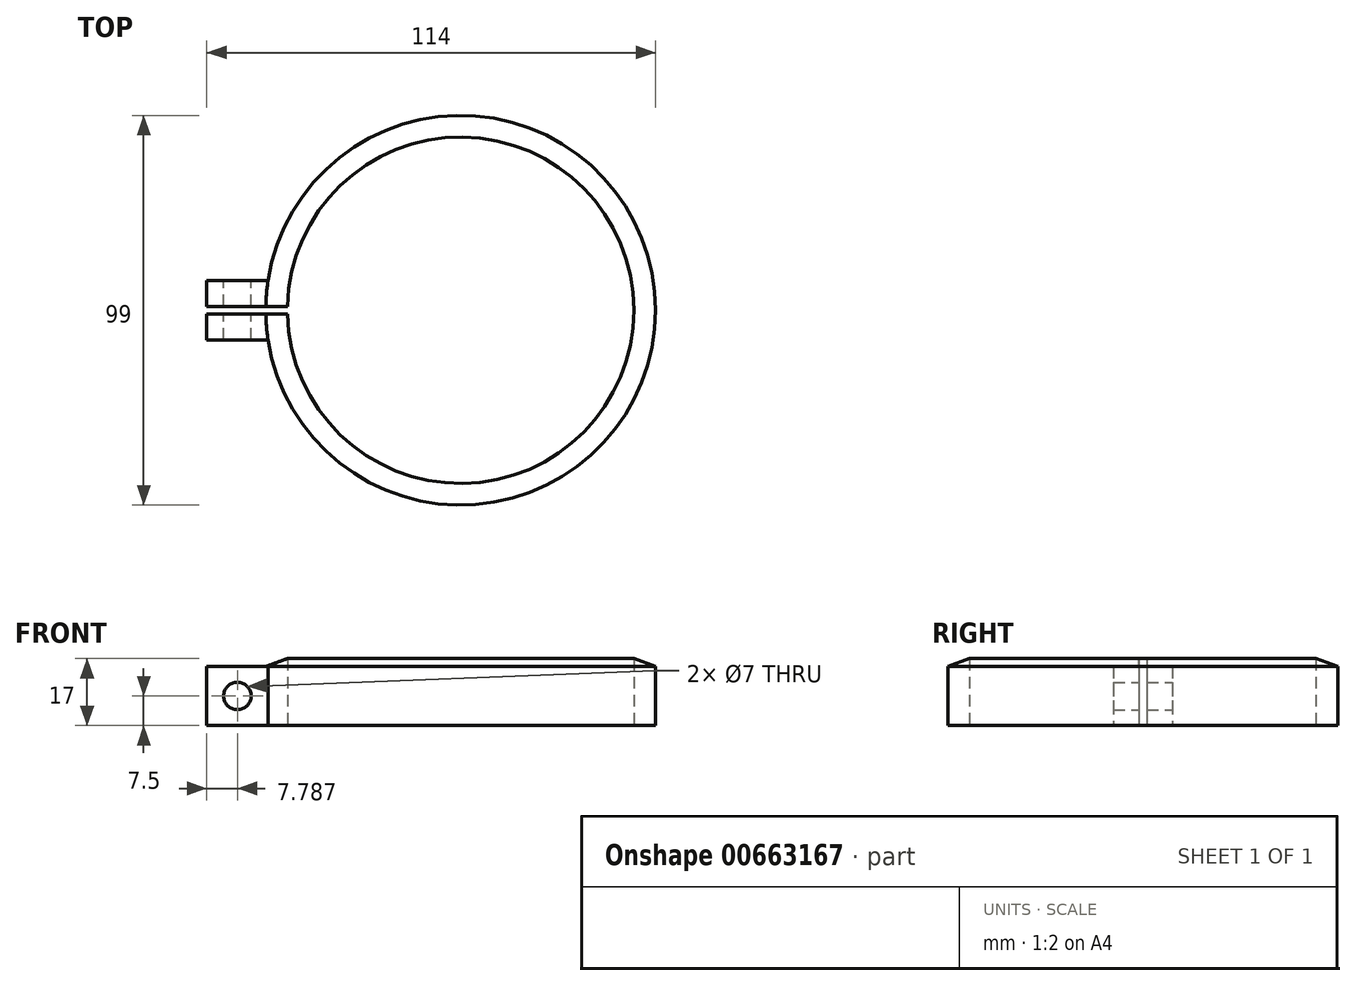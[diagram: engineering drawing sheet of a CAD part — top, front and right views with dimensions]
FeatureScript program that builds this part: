
annotation { "Feature Type Name" : "Feature", "Feature Type Description" : "" }
export const myFeature = defineFeature(function(context is Context, id is Id, definition is map)
    precondition{}
    {
        {
            var Q0;
            Q0=qCreatedBy(makeId("Top.planeOp"),FACE);
            var sketch = newSketch(context, id + "F0", { "sketchPlane" : qUnion([Q0])});
            skCircle(sketch, "E0", {"center": v(0, 0) * mm, "radius": 44 * mm, "construction": true});
            skCircle(sketch, "E1", {"center": v(0, 0) * mm, "radius": 49.5 * mm, "construction": true});
            skLineSegment(sketch, "E2", {"start": v(0, 0) * mm, "end": v(-49.5, 0) * mm, "construction": true});
            skLineSegment(sketch, "E3", {"start": v(-43.99, 1) * mm, "end": v(-43.99, 0) * mm, "construction": true});
            skLineSegment(sketch, "E4", {"start": v(-43.99, 1) * mm, "end": v(-49.49, 1) * mm, "construction": true});
            skLineSegment(sketch, "E5", {"start": v(-43.99, 1) * mm, "end": v(-43.99, -1) * mm, "construction": true});
            skLineSegment(sketch, "E6", {"start": v(-43.99, -1) * mm, "end": v(-49.49, -1) * mm, "construction": true});
            skLineSegment(sketch, "E7", {"start": v(-64.5, 1) * mm, "end": v(-64.5, 7.5) * mm});
            skLineSegment(sketch, "E8", {"start": v(-64.5, 7.5) * mm, "end": v(-48.93, 7.5) * mm});
            skLineSegment(sketch, "E9", {"start": v(-64.5, -1) * mm, "end": v(-64.5, -7.5) * mm});
            skLineSegment(sketch, "E10", {"start": v(-64.5, -7.5) * mm, "end": v(-48.93, -7.5) * mm});
            skArc(sketch, "E11", {"start": v(-48.93, -7.5) * mm, "mid": v(49.5, 0) * mm, "end": v(-48.93, 7.5) * mm});
            skLineSegment(sketch, "E12", {"start": v(-64.5, 1) * mm, "end": v(-43.99, 1) * mm});
            skLineSegment(sketch, "E13", {"start": v(-64.5, -1) * mm, "end": v(-43.99, -1) * mm});
            skArc(sketch, "E14", {"start": v(-43.99, -1) * mm, "mid": v(44, 0) * mm, "end": v(-43.99, 1) * mm});
            skSolve(sketch);
        }
        {
            var Q0;
            Q0 = qSketchRegion(id + "F0", true);
            extrude(context, id + "F1", {"entities" : qUnion([Q0]), "depth" : 15 * mm, "offsetDistance" : 25 * mm});
        }
        {
            var Q0;
            Q0=makeQuery(id+"F1.opExtrude","SWEPT_FACE",FACE,{"disambiguationData":[OSD([sQuery(id+"F0.wireOp",EDGE,"E12")])]});
            var sketch = newSketch(context, id + "F2", { "sketchPlane" : qUnion([Q0])});
            skLineSegment(sketch, "E15", {"start": v(-43.99, 15) * mm, "end": v(-49.49, 15) * mm});
            skLineSegment(sketch, "E16", {"start": v(-43.99, 15) * mm, "end": v(-43.99, 17) * mm});
            skLineSegment(sketch, "E17", {"start": v(-43.99, 17) * mm, "end": v(-49.49, 15) * mm});
            skSolve(sketch);
        }
        {
            var Q0;
            Q0=makeQuery(id+"F2.imprint","IMPRINT",FACE,{"disambiguationData":[TD([[makeQuery(id+"F2.imprint","IMPRINT",EDGE,{"derivedFrom":sQuery(id+"F2.wireOp",EDGE,"E15")}),1.0]])]});
            var Q1;
            Q1=makeQuery(id+"F1.opExtrude","SWEPT_FACE",FACE,{"disambiguationData":[OSD([sQuery(id+"F0.wireOp",EDGE,"E14")])]});
            revolve(context, id + "F3", {"operationType" : NewBodyOperationType.ADD, "surfaceOperationType" : NewSurfaceOperationType.NEW, "entities" : qUnion([Q0]), "axis" : qUnion([Q1]), "revolveType" : RevolveType.FULL});
        }
        {
            var Q0;
            Q0=makeQuery(id+"F3.opRevolve","SWEPT_FACE",FACE,{"disambiguationData":[OSD([sQuery(id+"F2.wireOp",EDGE,"E15")])]});
            var sketch = newSketch(context, id + "F4", { "sketchPlane" : qUnion([Q0])});
            skLineSegment(sketch, "E18.bottom", {"start": v(-49.49, 1) * mm, "end": v(-43.99, 1) * mm});
            skLineSegment(sketch, "E18.top", {"start": v(-49.49, -1) * mm, "end": v(-43.99, -1) * mm});
            skLineSegment(sketch, "E18.left", {"start": v(-49.49, 1) * mm, "end": v(-49.49, -1) * mm});
            skLineSegment(sketch, "E18.right", {"start": v(-43.99, 1) * mm, "end": v(-43.99, -1) * mm});
            skSolve(sketch);
        }
        {
            var Q0;
            Q0 = qSketchRegion(id + "F4", true);
            extrude(context, id + "F5", {"entities" : qUnion([Q0]), "operationType" : NewBodyOperationType.REMOVE, "oppositeDirection" : true, "depth" : 25 * mm, "offsetDistance" : 25 * mm});
        }
        {
            var Q0;
            Q0=makeQuery(id+"F1.opExtrude","SWEPT_FACE",FACE,{"disambiguationData":[OSD([sQuery(id+"F0.wireOp",EDGE,"E8")])]});
            var sketch = newSketch(context, id + "F6", { "sketchPlane" : qUnion([Q0])});
            skLineSegment(sketch, "E19", {"start": v(64.5, 7.5) * mm, "end": v(48.93, 7.5) * mm, "construction": true});
            skLineSegment(sketch, "E20", {"start": v(56.71, 15) * mm, "end": v(56.71, 0) * mm, "construction": true});
            skCircle(sketch, "E21", {"center": v(56.71, 7.5) * mm, "radius": 3.5 * mm});
            skSolve(sketch);
        }
        {
            var Q0;
            Q0 = qSketchRegion(id + "F6", true);
            extrude(context, id + "F7", {"entities" : qUnion([Q0]), "operationType" : NewBodyOperationType.REMOVE, "oppositeDirection" : true, "depth" : 25 * mm, "offsetDistance" : 25 * mm});
        }
    });
